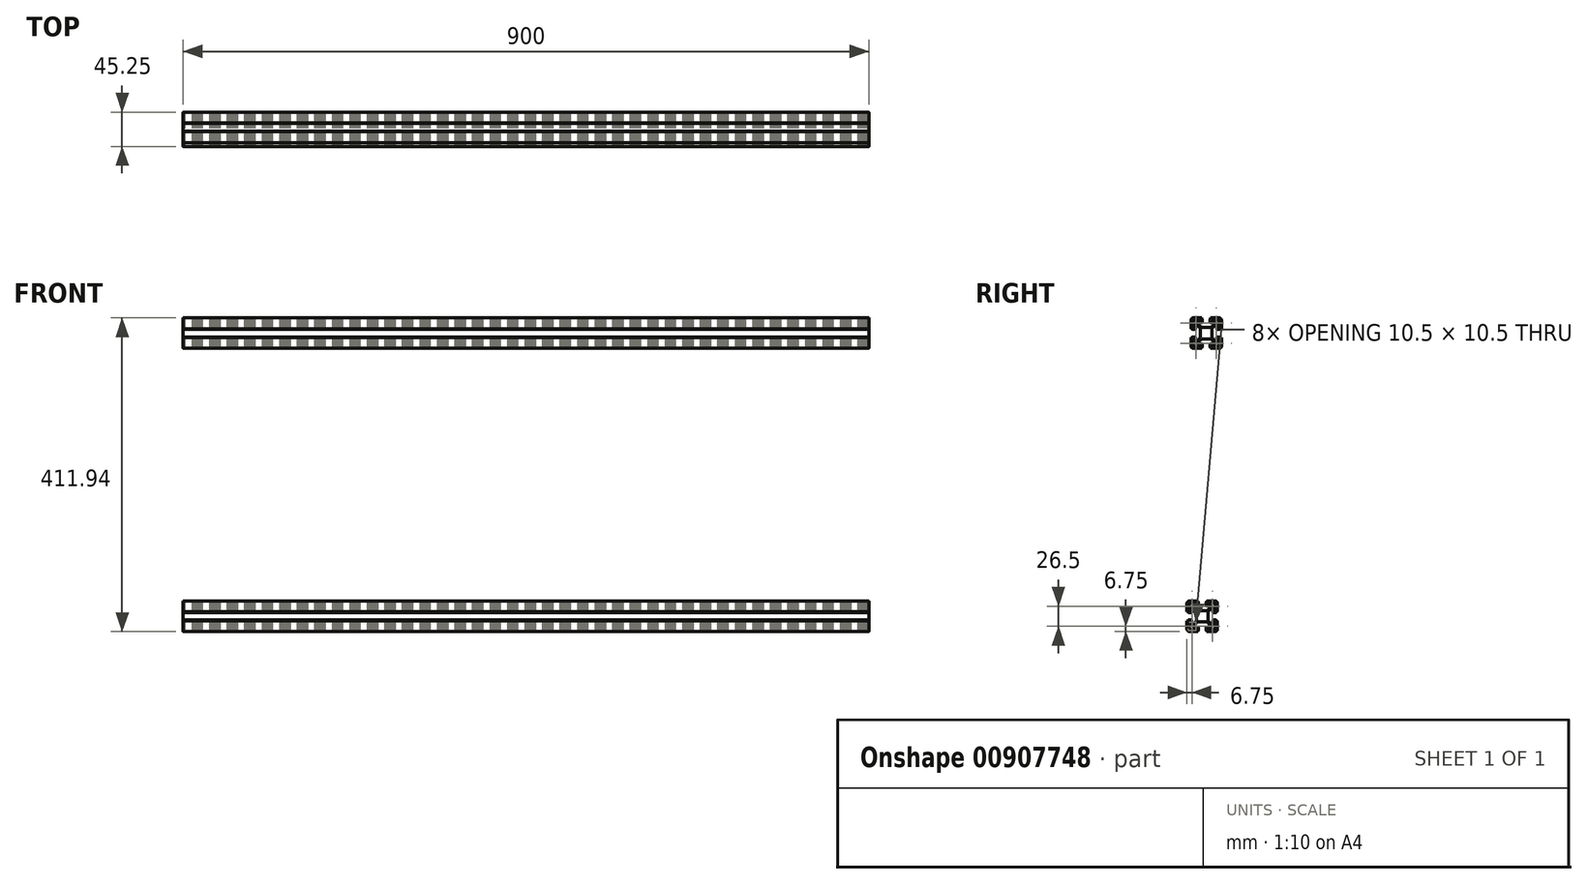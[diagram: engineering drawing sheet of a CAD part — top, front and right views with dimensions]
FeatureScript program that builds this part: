
annotation { "Feature Type Name" : "Feature", "Feature Type Description" : "" }
export const myFeature = defineFeature(function(context is Context, id is Id, definition is map)
    precondition{}
    {
        {
            var Q0;
            Q0=qCreatedBy(makeId("Right.planeOp"),FACE);
            var sketch = newSketch(context, id + "F0", { "sketchPlane" : qUnion([Q0])});
            skLineSegment(sketch, "E0", {"start": v(5.8, -18.5) * mm, "end": v(5.8, -20) * mm});
            skLineSegment(sketch, "E1", {"start": v(5.8, -20) * mm, "end": v(17, -20) * mm});
            skArc(sketch, "E2", {"start": v(17, -20) * mm, "mid": v(19.12, -19.12) * mm, "end": v(20, -17) * mm});
            skLineSegment(sketch, "E3", {"start": v(20, -17) * mm, "end": v(20, -5.8) * mm});
            skLineSegment(sketch, "E4", {"start": v(20, -5.8) * mm, "end": v(18.5, -5.8) * mm});
            skLineSegment(sketch, "E5", {"start": v(18.5, -5.8) * mm, "end": v(18.5, -5) * mm});
            skLineSegment(sketch, "E6", {"start": v(18.5, -5) * mm, "end": v(14, -5) * mm});
            skLineSegment(sketch, "E7", {"start": v(14, -5) * mm, "end": v(14, -10.05) * mm});
            skLineSegment(sketch, "E8", {"start": v(14, -10.05) * mm, "end": v(11.46, -10.05) * mm});
            skLineSegment(sketch, "E9", {"start": v(11.46, -10.05) * mm, "end": v(7.5, -6.09) * mm});
            skLineSegment(sketch, "E10", {"start": v(7.5, -6.09) * mm, "end": v(7.5, 6.09) * mm});
            skLineSegment(sketch, "E11", {"start": v(7.5, 6.09) * mm, "end": v(11.46, 10.05) * mm});
            skLineSegment(sketch, "E12", {"start": v(11.46, 10.05) * mm, "end": v(14, 10.05) * mm});
            skLineSegment(sketch, "E13", {"start": v(14, 10.05) * mm, "end": v(14, 5) * mm});
            skLineSegment(sketch, "E14", {"start": v(14, 5) * mm, "end": v(18.5, 5) * mm});
            skLineSegment(sketch, "E15", {"start": v(18.5, 5) * mm, "end": v(18.5, 5.8) * mm});
            skLineSegment(sketch, "E16", {"start": v(18.5, 5.8) * mm, "end": v(20, 5.8) * mm});
            skLineSegment(sketch, "E17", {"start": v(20, 5.8) * mm, "end": v(20, 17) * mm});
            skArc(sketch, "E18", {"start": v(20, 17) * mm, "mid": v(19.12, 19.12) * mm, "end": v(17, 20) * mm});
            skLineSegment(sketch, "E19", {"start": v(17, 20) * mm, "end": v(5.8, 20) * mm});
            skLineSegment(sketch, "E20", {"start": v(5.8, 20) * mm, "end": v(5.8, 18.5) * mm});
            skLineSegment(sketch, "E21", {"start": v(5.8, 18.5) * mm, "end": v(5, 18.5) * mm});
            skLineSegment(sketch, "E22", {"start": v(5, 18.5) * mm, "end": v(5, 14) * mm});
            skLineSegment(sketch, "E23", {"start": v(5, 14) * mm, "end": v(10.05, 14) * mm});
            skLineSegment(sketch, "E24", {"start": v(10.05, 14) * mm, "end": v(10.05, 11.46) * mm});
            skLineSegment(sketch, "E25", {"start": v(10.05, 11.46) * mm, "end": v(6.09, 7.5) * mm});
            skLineSegment(sketch, "E26", {"start": v(6.09, 7.5) * mm, "end": v(-6.09, 7.5) * mm});
            skLineSegment(sketch, "E27", {"start": v(-6.09, 7.5) * mm, "end": v(-10.05, 11.46) * mm});
            skLineSegment(sketch, "E28", {"start": v(-10.05, 11.46) * mm, "end": v(-10.05, 14) * mm});
            skLineSegment(sketch, "E29", {"start": v(-10.05, 14) * mm, "end": v(-5, 14) * mm});
            skLineSegment(sketch, "E30", {"start": v(-5, 14) * mm, "end": v(-5, 18.5) * mm});
            skLineSegment(sketch, "E31", {"start": v(-5, 18.5) * mm, "end": v(-5.8, 18.5) * mm});
            skLineSegment(sketch, "E32", {"start": v(-5.8, 18.5) * mm, "end": v(-5.8, 20) * mm});
            skLineSegment(sketch, "E33", {"start": v(-5.8, 20) * mm, "end": v(-17, 20) * mm});
            skArc(sketch, "E34", {"start": v(-17, 20) * mm, "mid": v(-19.12, 19.12) * mm, "end": v(-20, 17) * mm});
            skLineSegment(sketch, "E35", {"start": v(-20, 17) * mm, "end": v(-20, 5.8) * mm});
            skLineSegment(sketch, "E36", {"start": v(-20, 5.8) * mm, "end": v(-18.5, 5.8) * mm});
            skLineSegment(sketch, "E37", {"start": v(-18.5, 5.8) * mm, "end": v(-18.5, 5) * mm});
            skLineSegment(sketch, "E38", {"start": v(-18.5, 5) * mm, "end": v(-14, 5) * mm});
            skLineSegment(sketch, "E39", {"start": v(-14, 5) * mm, "end": v(-14, 10.05) * mm});
            skLineSegment(sketch, "E40", {"start": v(-14, 10.05) * mm, "end": v(-11.46, 10.05) * mm});
            skLineSegment(sketch, "E41", {"start": v(-11.46, 10.05) * mm, "end": v(-7.5, 6.09) * mm});
            skLineSegment(sketch, "E42", {"start": v(-7.5, 6.09) * mm, "end": v(-7.5, -6.09) * mm});
            skLineSegment(sketch, "E43", {"start": v(-7.5, -6.09) * mm, "end": v(-11.46, -10.05) * mm});
            skLineSegment(sketch, "E44", {"start": v(-11.46, -10.05) * mm, "end": v(-14, -10.05) * mm});
            skLineSegment(sketch, "E45", {"start": v(-14, -10.05) * mm, "end": v(-14, -5) * mm});
            skLineSegment(sketch, "E46", {"start": v(-14, -5) * mm, "end": v(-18.5, -5) * mm});
            skLineSegment(sketch, "E47", {"start": v(-18.5, -5) * mm, "end": v(-18.5, -5.8) * mm});
            skLineSegment(sketch, "E48", {"start": v(-18.5, -5.8) * mm, "end": v(-20, -5.8) * mm});
            skLineSegment(sketch, "E49", {"start": v(-20, -5.8) * mm, "end": v(-20, -17) * mm});
            skArc(sketch, "E50", {"start": v(-20, -17) * mm, "mid": v(-19.12, -19.12) * mm, "end": v(-17, -20) * mm});
            skLineSegment(sketch, "E51", {"start": v(-17, -20) * mm, "end": v(-5.8, -20) * mm});
            skLineSegment(sketch, "E52", {"start": v(-5.8, -20) * mm, "end": v(-5.8, -18.5) * mm});
            skLineSegment(sketch, "E53", {"start": v(-5.8, -18.5) * mm, "end": v(-5, -18.5) * mm});
            skLineSegment(sketch, "E54", {"start": v(-5, -18.5) * mm, "end": v(-5, -14) * mm});
            skLineSegment(sketch, "E55", {"start": v(-5, -14) * mm, "end": v(-10.05, -14) * mm});
            skLineSegment(sketch, "E56", {"start": v(-10.05, -14) * mm, "end": v(-10.05, -11.46) * mm});
            skLineSegment(sketch, "E57", {"start": v(-10.05, -11.46) * mm, "end": v(-6.09, -7.5) * mm});
            skLineSegment(sketch, "E58", {"start": v(-6.09, -7.5) * mm, "end": v(6.09, -7.5) * mm});
            skLineSegment(sketch, "E59", {"start": v(6.09, -7.5) * mm, "end": v(10.05, -11.46) * mm});
            skLineSegment(sketch, "E60", {"start": v(10.05, -11.46) * mm, "end": v(10.05, -14) * mm});
            skLineSegment(sketch, "E61", {"start": v(10.05, -14) * mm, "end": v(5, -14) * mm});
            skLineSegment(sketch, "E62", {"start": v(5, -14) * mm, "end": v(5, -18.5) * mm});
            skLineSegment(sketch, "E63", {"start": v(5, -18.5) * mm, "end": v(5.8, -18.5) * mm});
            skLineSegment(sketch, "E64", {"start": v(18.5, 9.5) * mm, "end": v(18.5, 14.5) * mm});
            skArc(sketch, "E65", {"start": v(15.5, 9.5) * mm, "mid": v(17, 8) * mm, "end": v(18.5, 9.5) * mm});
            skLineSegment(sketch, "E66", {"start": v(15.5, 11.75) * mm, "end": v(15.5, 9.5) * mm});
            skLineSegment(sketch, "E67", {"start": v(14.5, 11.75) * mm, "end": v(15.5, 11.75) * mm});
            skArc(sketch, "E68", {"start": v(11.75, 14.5) * mm, "mid": v(12.56, 12.56) * mm, "end": v(14.5, 11.75) * mm});
            skLineSegment(sketch, "E69", {"start": v(11.75, 15.5) * mm, "end": v(11.75, 14.5) * mm});
            skLineSegment(sketch, "E70", {"start": v(9.5, 15.5) * mm, "end": v(11.75, 15.5) * mm});
            skArc(sketch, "E71", {"start": v(9.5, 18.5) * mm, "mid": v(8, 17) * mm, "end": v(9.5, 15.5) * mm});
            skLineSegment(sketch, "E72", {"start": v(14.5, 18.5) * mm, "end": v(9.5, 18.5) * mm});
            skLineSegment(sketch, "E73", {"start": v(14.5, 17.25) * mm, "end": v(14.5, 18.5) * mm});
            skArc(sketch, "E74", {"start": v(17.25, 14.5) * mm, "mid": v(16.44, 16.44) * mm, "end": v(14.5, 17.25) * mm});
            skLineSegment(sketch, "E75", {"start": v(18.5, 14.5) * mm, "end": v(17.25, 14.5) * mm});
            skLineSegment(sketch, "E76", {"start": v(11.75, -14.5) * mm, "end": v(11.75, -15.5) * mm});
            skArc(sketch, "E77", {"start": v(14.5, -11.75) * mm, "mid": v(12.56, -12.56) * mm, "end": v(11.75, -14.5) * mm});
            skLineSegment(sketch, "E78", {"start": v(15.5, -11.75) * mm, "end": v(14.5, -11.75) * mm});
            skLineSegment(sketch, "E79", {"start": v(15.5, -9.5) * mm, "end": v(15.5, -11.75) * mm});
            skArc(sketch, "E80", {"start": v(18.5, -9.5) * mm, "mid": v(17, -8) * mm, "end": v(15.5, -9.5) * mm});
            skLineSegment(sketch, "E81", {"start": v(18.5, -14.5) * mm, "end": v(18.5, -9.5) * mm});
            skLineSegment(sketch, "E82", {"start": v(17.25, -14.5) * mm, "end": v(18.5, -14.5) * mm});
            skArc(sketch, "E83", {"start": v(14.5, -17.25) * mm, "mid": v(16.44, -16.44) * mm, "end": v(17.25, -14.5) * mm});
            skLineSegment(sketch, "E84", {"start": v(14.5, -18.5) * mm, "end": v(14.5, -17.25) * mm});
            skLineSegment(sketch, "E85", {"start": v(9.5, -18.5) * mm, "end": v(14.5, -18.5) * mm});
            skArc(sketch, "E86", {"start": v(9.5, -15.5) * mm, "mid": v(8, -17) * mm, "end": v(9.5, -18.5) * mm});
            skLineSegment(sketch, "E87", {"start": v(11.75, -15.5) * mm, "end": v(9.5, -15.5) * mm});
            skLineSegment(sketch, "E88", {"start": v(-2, 4.58) * mm, "end": v(-2.4, 5.5) * mm});
            skLineSegment(sketch, "E89", {"start": v(2.4, 5.5) * mm, "end": v(2, 4.58) * mm});
            skLineSegment(sketch, "E90", {"start": v(5.5, 5.5) * mm, "end": v(2.4, 5.5) * mm});
            skLineSegment(sketch, "E91", {"start": v(5.5, 2.4) * mm, "end": v(5.5, 5.5) * mm});
            skLineSegment(sketch, "E92", {"start": v(4.58, 2) * mm, "end": v(5.5, 2.4) * mm});
            skArc(sketch, "E93", {"start": v(4.58, -2) * mm, "mid": v(5, 0) * mm, "end": v(4.58, 2) * mm});
            skLineSegment(sketch, "E94", {"start": v(5.5, -2.4) * mm, "end": v(4.58, -2) * mm});
            skLineSegment(sketch, "E95", {"start": v(5.5, -5.5) * mm, "end": v(5.5, -2.4) * mm});
            skLineSegment(sketch, "E96", {"start": v(2.4, -5.5) * mm, "end": v(5.5, -5.5) * mm});
            skLineSegment(sketch, "E97", {"start": v(2, -4.58) * mm, "end": v(2.4, -5.5) * mm});
            skArc(sketch, "E98", {"start": v(-2, -4.58) * mm, "mid": v(0, -5) * mm, "end": v(2, -4.58) * mm});
            skLineSegment(sketch, "E99", {"start": v(-2.4, -5.5) * mm, "end": v(-2, -4.58) * mm});
            skLineSegment(sketch, "E100", {"start": v(-5.5, -5.5) * mm, "end": v(-2.4, -5.5) * mm});
            skLineSegment(sketch, "E101", {"start": v(-5.5, -2.4) * mm, "end": v(-5.5, -5.5) * mm});
            skLineSegment(sketch, "E102", {"start": v(-4.58, -2) * mm, "end": v(-5.5, -2.4) * mm});
            skArc(sketch, "E103", {"start": v(-4.58, 2) * mm, "mid": v(-5, 0) * mm, "end": v(-4.58, -2) * mm});
            skLineSegment(sketch, "E104", {"start": v(-5.5, 2.4) * mm, "end": v(-4.58, 2) * mm});
            skLineSegment(sketch, "E105", {"start": v(-5.5, 5.5) * mm, "end": v(-5.5, 2.4) * mm});
            skLineSegment(sketch, "E106", {"start": v(-2.4, 5.5) * mm, "end": v(-5.5, 5.5) * mm});
            skLineSegment(sketch, "E107", {"start": v(-18.5, -9.5) * mm, "end": v(-18.5, -14.5) * mm});
            skArc(sketch, "E108", {"start": v(-15.5, -9.5) * mm, "mid": v(-17, -8) * mm, "end": v(-18.5, -9.5) * mm});
            skLineSegment(sketch, "E109", {"start": v(-15.5, -11.75) * mm, "end": v(-15.5, -9.5) * mm});
            skLineSegment(sketch, "E110", {"start": v(-14.5, -11.75) * mm, "end": v(-15.5, -11.75) * mm});
            skArc(sketch, "E111", {"start": v(-11.75, -14.5) * mm, "mid": v(-12.56, -12.56) * mm, "end": v(-14.5, -11.75) * mm});
            skLineSegment(sketch, "E112", {"start": v(-11.75, -15.5) * mm, "end": v(-11.75, -14.5) * mm});
            skLineSegment(sketch, "E113", {"start": v(-9.5, -15.5) * mm, "end": v(-11.75, -15.5) * mm});
            skArc(sketch, "E114", {"start": v(-9.5, -18.5) * mm, "mid": v(-8, -17) * mm, "end": v(-9.5, -15.5) * mm});
            skLineSegment(sketch, "E115", {"start": v(-14.5, -18.5) * mm, "end": v(-9.5, -18.5) * mm});
            skLineSegment(sketch, "E116", {"start": v(-14.5, -17.25) * mm, "end": v(-14.5, -18.5) * mm});
            skArc(sketch, "E117", {"start": v(-17.25, -14.5) * mm, "mid": v(-16.44, -16.44) * mm, "end": v(-14.5, -17.25) * mm});
            skLineSegment(sketch, "E118", {"start": v(-18.5, -14.5) * mm, "end": v(-17.25, -14.5) * mm});
            skLineSegment(sketch, "E119", {"start": v(-11.75, 14.5) * mm, "end": v(-11.75, 15.5) * mm});
            skArc(sketch, "E120", {"start": v(-14.5, 11.75) * mm, "mid": v(-12.56, 12.56) * mm, "end": v(-11.75, 14.5) * mm});
            skLineSegment(sketch, "E121", {"start": v(-15.5, 11.75) * mm, "end": v(-14.5, 11.75) * mm});
            skLineSegment(sketch, "E122", {"start": v(-15.5, 9.5) * mm, "end": v(-15.5, 11.75) * mm});
            skArc(sketch, "E123", {"start": v(-18.5, 9.5) * mm, "mid": v(-17, 8) * mm, "end": v(-15.5, 9.5) * mm});
            skLineSegment(sketch, "E124", {"start": v(-18.5, 14.5) * mm, "end": v(-18.5, 9.5) * mm});
            skLineSegment(sketch, "E125", {"start": v(-17.25, 14.5) * mm, "end": v(-18.5, 14.5) * mm});
            skArc(sketch, "E126", {"start": v(-14.5, 17.25) * mm, "mid": v(-16.44, 16.44) * mm, "end": v(-17.25, 14.5) * mm});
            skLineSegment(sketch, "E127", {"start": v(-14.5, 18.5) * mm, "end": v(-14.5, 17.25) * mm});
            skLineSegment(sketch, "E128", {"start": v(-9.5, 18.5) * mm, "end": v(-14.5, 18.5) * mm});
            skArc(sketch, "E129", {"start": v(-9.5, 15.5) * mm, "mid": v(-8, 17) * mm, "end": v(-9.5, 18.5) * mm});
            skLineSegment(sketch, "E130", {"start": v(-11.75, 15.5) * mm, "end": v(-9.5, 15.5) * mm});
            skLineSegment(sketch, "E131", {"start": v(11.05, 353.44) * mm, "end": v(11.05, 351.94) * mm});
            skLineSegment(sketch, "E132", {"start": v(11.05, 351.94) * mm, "end": v(22.25, 351.94) * mm});
            skArc(sketch, "E133", {"start": v(22.25, 351.94) * mm, "mid": v(24.37, 352.82) * mm, "end": v(25.25, 354.94) * mm});
            skLineSegment(sketch, "E134", {"start": v(25.25, 354.94) * mm, "end": v(25.25, 366.14) * mm});
            skLineSegment(sketch, "E135", {"start": v(25.25, 366.14) * mm, "end": v(23.75, 366.14) * mm});
            skLineSegment(sketch, "E136", {"start": v(23.75, 366.14) * mm, "end": v(23.75, 366.94) * mm});
            skLineSegment(sketch, "E137", {"start": v(23.75, 366.94) * mm, "end": v(19.25, 366.94) * mm});
            skLineSegment(sketch, "E138", {"start": v(19.25, 366.94) * mm, "end": v(19.25, 361.89) * mm});
            skLineSegment(sketch, "E139", {"start": v(19.25, 361.89) * mm, "end": v(16.71, 361.89) * mm});
            skLineSegment(sketch, "E140", {"start": v(16.71, 361.89) * mm, "end": v(12.75, 365.85) * mm});
            skLineSegment(sketch, "E141", {"start": v(12.75, 365.85) * mm, "end": v(12.75, 378.02) * mm});
            skLineSegment(sketch, "E142", {"start": v(12.75, 378.02) * mm, "end": v(16.71, 381.99) * mm});
            skLineSegment(sketch, "E143", {"start": v(16.71, 381.99) * mm, "end": v(19.25, 381.99) * mm});
            skLineSegment(sketch, "E144", {"start": v(19.25, 381.99) * mm, "end": v(19.25, 376.94) * mm});
            skLineSegment(sketch, "E145", {"start": v(19.25, 376.94) * mm, "end": v(23.75, 376.94) * mm});
            skLineSegment(sketch, "E146", {"start": v(23.75, 376.94) * mm, "end": v(23.75, 377.74) * mm});
            skLineSegment(sketch, "E147", {"start": v(23.75, 377.74) * mm, "end": v(25.25, 377.74) * mm});
            skLineSegment(sketch, "E148", {"start": v(25.25, 377.74) * mm, "end": v(25.25, 388.94) * mm});
            skArc(sketch, "E149", {"start": v(25.25, 388.94) * mm, "mid": v(24.37, 391.06) * mm, "end": v(22.25, 391.94) * mm});
            skLineSegment(sketch, "E150", {"start": v(22.25, 391.94) * mm, "end": v(11.05, 391.94) * mm});
            skLineSegment(sketch, "E151", {"start": v(11.05, 391.94) * mm, "end": v(11.05, 390.44) * mm});
            skLineSegment(sketch, "E152", {"start": v(11.05, 390.44) * mm, "end": v(10.25, 390.44) * mm});
            skLineSegment(sketch, "E153", {"start": v(10.25, 390.44) * mm, "end": v(10.25, 385.94) * mm});
            skLineSegment(sketch, "E154", {"start": v(10.25, 385.94) * mm, "end": v(15.3, 385.94) * mm});
            skLineSegment(sketch, "E155", {"start": v(15.3, 385.94) * mm, "end": v(15.3, 383.4) * mm});
            skLineSegment(sketch, "E156", {"start": v(15.3, 383.4) * mm, "end": v(11.34, 379.44) * mm});
            skLineSegment(sketch, "E157", {"start": v(11.34, 379.44) * mm, "end": v(-0.84, 379.44) * mm});
            skLineSegment(sketch, "E158", {"start": v(-0.84, 379.44) * mm, "end": v(-4.8, 383.4) * mm});
            skLineSegment(sketch, "E159", {"start": v(-4.8, 383.4) * mm, "end": v(-4.8, 385.94) * mm});
            skLineSegment(sketch, "E160", {"start": v(-4.8, 385.94) * mm, "end": v(0.25, 385.94) * mm});
            skLineSegment(sketch, "E161", {"start": v(0.25, 385.94) * mm, "end": v(0.25, 390.44) * mm});
            skLineSegment(sketch, "E162", {"start": v(0.25, 390.44) * mm, "end": v(-0.55, 390.44) * mm});
            skLineSegment(sketch, "E163", {"start": v(-0.55, 390.44) * mm, "end": v(-0.55, 391.94) * mm});
            skLineSegment(sketch, "E164", {"start": v(-0.55, 391.94) * mm, "end": v(-11.75, 391.94) * mm});
            skArc(sketch, "E165", {"start": v(-11.75, 391.94) * mm, "mid": v(-13.87, 391.06) * mm, "end": v(-14.75, 388.94) * mm});
            skLineSegment(sketch, "E166", {"start": v(-14.75, 388.94) * mm, "end": v(-14.75, 377.74) * mm});
            skLineSegment(sketch, "E167", {"start": v(-14.75, 377.74) * mm, "end": v(-13.25, 377.74) * mm});
            skLineSegment(sketch, "E168", {"start": v(-13.25, 377.74) * mm, "end": v(-13.25, 376.94) * mm});
            skLineSegment(sketch, "E169", {"start": v(-13.25, 376.94) * mm, "end": v(-8.75, 376.94) * mm});
            skLineSegment(sketch, "E170", {"start": v(-8.75, 376.94) * mm, "end": v(-8.75, 381.99) * mm});
            skLineSegment(sketch, "E171", {"start": v(-8.75, 381.99) * mm, "end": v(-6.21, 381.99) * mm});
            skLineSegment(sketch, "E172", {"start": v(-6.21, 381.99) * mm, "end": v(-2.25, 378.02) * mm});
            skLineSegment(sketch, "E173", {"start": v(-2.25, 378.02) * mm, "end": v(-2.25, 365.85) * mm});
            skLineSegment(sketch, "E174", {"start": v(-2.25, 365.85) * mm, "end": v(-6.21, 361.89) * mm});
            skLineSegment(sketch, "E175", {"start": v(-6.21, 361.89) * mm, "end": v(-8.75, 361.89) * mm});
            skLineSegment(sketch, "E176", {"start": v(-8.75, 361.89) * mm, "end": v(-8.75, 366.94) * mm});
            skLineSegment(sketch, "E177", {"start": v(-8.75, 366.94) * mm, "end": v(-13.25, 366.94) * mm});
            skLineSegment(sketch, "E178", {"start": v(-13.25, 366.94) * mm, "end": v(-13.25, 366.14) * mm});
            skLineSegment(sketch, "E179", {"start": v(-13.25, 366.14) * mm, "end": v(-14.75, 366.14) * mm});
            skLineSegment(sketch, "E180", {"start": v(-14.75, 366.14) * mm, "end": v(-14.75, 354.94) * mm});
            skArc(sketch, "E181", {"start": v(-14.75, 354.94) * mm, "mid": v(-13.87, 352.82) * mm, "end": v(-11.75, 351.94) * mm});
            skLineSegment(sketch, "E182", {"start": v(-11.75, 351.94) * mm, "end": v(-0.55, 351.94) * mm});
            skLineSegment(sketch, "E183", {"start": v(-0.55, 351.94) * mm, "end": v(-0.55, 353.44) * mm});
            skLineSegment(sketch, "E184", {"start": v(-0.55, 353.44) * mm, "end": v(0.25, 353.44) * mm});
            skLineSegment(sketch, "E185", {"start": v(0.25, 353.44) * mm, "end": v(0.25, 357.94) * mm});
            skLineSegment(sketch, "E186", {"start": v(0.25, 357.94) * mm, "end": v(-4.8, 357.94) * mm});
            skLineSegment(sketch, "E187", {"start": v(-4.8, 357.94) * mm, "end": v(-4.8, 360.47) * mm});
            skLineSegment(sketch, "E188", {"start": v(-4.8, 360.47) * mm, "end": v(-0.84, 364.44) * mm});
            skLineSegment(sketch, "E189", {"start": v(-0.84, 364.44) * mm, "end": v(11.34, 364.44) * mm});
            skLineSegment(sketch, "E190", {"start": v(11.34, 364.44) * mm, "end": v(15.3, 360.47) * mm});
            skLineSegment(sketch, "E191", {"start": v(15.3, 360.47) * mm, "end": v(15.3, 357.94) * mm});
            skLineSegment(sketch, "E192", {"start": v(15.3, 357.94) * mm, "end": v(10.25, 357.94) * mm});
            skLineSegment(sketch, "E193", {"start": v(10.25, 357.94) * mm, "end": v(10.25, 353.44) * mm});
            skLineSegment(sketch, "E194", {"start": v(10.25, 353.44) * mm, "end": v(11.05, 353.44) * mm});
            skLineSegment(sketch, "E195", {"start": v(23.75, 381.44) * mm, "end": v(23.75, 386.44) * mm});
            skArc(sketch, "E196", {"start": v(20.75, 381.44) * mm, "mid": v(22.25, 379.94) * mm, "end": v(23.75, 381.44) * mm});
            skLineSegment(sketch, "E197", {"start": v(20.75, 383.69) * mm, "end": v(20.75, 381.44) * mm});
            skLineSegment(sketch, "E198", {"start": v(19.75, 383.69) * mm, "end": v(20.75, 383.69) * mm});
            skArc(sketch, "E199", {"start": v(17, 386.44) * mm, "mid": v(17.8, 384.5) * mm, "end": v(19.75, 383.69) * mm});
            skLineSegment(sketch, "E200", {"start": v(17, 387.44) * mm, "end": v(17, 386.44) * mm});
            skLineSegment(sketch, "E201", {"start": v(14.75, 387.44) * mm, "end": v(17, 387.44) * mm});
            skArc(sketch, "E202", {"start": v(14.75, 390.44) * mm, "mid": v(13.25, 388.94) * mm, "end": v(14.75, 387.44) * mm});
            skLineSegment(sketch, "E203", {"start": v(19.75, 390.44) * mm, "end": v(14.75, 390.44) * mm});
            skLineSegment(sketch, "E204", {"start": v(19.75, 389.19) * mm, "end": v(19.75, 390.44) * mm});
            skArc(sketch, "E205", {"start": v(22.5, 386.44) * mm, "mid": v(21.7, 388.38) * mm, "end": v(19.75, 389.19) * mm});
            skLineSegment(sketch, "E206", {"start": v(23.75, 386.44) * mm, "end": v(22.5, 386.44) * mm});
            skLineSegment(sketch, "E207", {"start": v(17, 357.44) * mm, "end": v(17, 356.44) * mm});
            skArc(sketch, "E208", {"start": v(19.75, 360.19) * mm, "mid": v(17.8, 359.38) * mm, "end": v(17, 357.44) * mm});
            skLineSegment(sketch, "E209", {"start": v(20.75, 360.19) * mm, "end": v(19.75, 360.19) * mm});
            skLineSegment(sketch, "E210", {"start": v(20.75, 362.44) * mm, "end": v(20.75, 360.19) * mm});
            skArc(sketch, "E211", {"start": v(23.75, 362.44) * mm, "mid": v(22.25, 363.94) * mm, "end": v(20.75, 362.44) * mm});
            skLineSegment(sketch, "E212", {"start": v(23.75, 357.44) * mm, "end": v(23.75, 362.44) * mm});
            skLineSegment(sketch, "E213", {"start": v(22.5, 357.44) * mm, "end": v(23.75, 357.44) * mm});
            skArc(sketch, "E214", {"start": v(19.75, 354.69) * mm, "mid": v(21.7, 355.5) * mm, "end": v(22.5, 357.44) * mm});
            skLineSegment(sketch, "E215", {"start": v(19.75, 353.44) * mm, "end": v(19.75, 354.69) * mm});
            skLineSegment(sketch, "E216", {"start": v(14.75, 353.44) * mm, "end": v(19.75, 353.44) * mm});
            skArc(sketch, "E217", {"start": v(14.75, 356.44) * mm, "mid": v(13.25, 354.94) * mm, "end": v(14.75, 353.44) * mm});
            skLineSegment(sketch, "E218", {"start": v(17, 356.44) * mm, "end": v(14.75, 356.44) * mm});
            skLineSegment(sketch, "E219", {"start": v(3.25, 376.52) * mm, "end": v(2.85, 377.44) * mm});
            skLineSegment(sketch, "E220", {"start": v(7.65, 377.44) * mm, "end": v(7.25, 376.52) * mm});
            skLineSegment(sketch, "E221", {"start": v(10.75, 377.44) * mm, "end": v(7.65, 377.44) * mm});
            skLineSegment(sketch, "E222", {"start": v(10.75, 374.34) * mm, "end": v(10.75, 377.44) * mm});
            skLineSegment(sketch, "E223", {"start": v(9.83, 373.94) * mm, "end": v(10.75, 374.34) * mm});
            skArc(sketch, "E224", {"start": v(9.83, 369.94) * mm, "mid": v(10.25, 371.94) * mm, "end": v(9.83, 373.94) * mm});
            skLineSegment(sketch, "E225", {"start": v(10.75, 369.54) * mm, "end": v(9.83, 369.94) * mm});
            skLineSegment(sketch, "E226", {"start": v(10.75, 366.44) * mm, "end": v(10.75, 369.54) * mm});
            skLineSegment(sketch, "E227", {"start": v(7.65, 366.44) * mm, "end": v(10.75, 366.44) * mm});
            skLineSegment(sketch, "E228", {"start": v(7.25, 367.36) * mm, "end": v(7.65, 366.44) * mm});
            skArc(sketch, "E229", {"start": v(3.25, 367.36) * mm, "mid": v(5.25, 366.94) * mm, "end": v(7.25, 367.36) * mm});
            skLineSegment(sketch, "E230", {"start": v(2.85, 366.44) * mm, "end": v(3.25, 367.36) * mm});
            skLineSegment(sketch, "E231", {"start": v(-0.25, 366.44) * mm, "end": v(2.85, 366.44) * mm});
            skLineSegment(sketch, "E232", {"start": v(-0.25, 369.54) * mm, "end": v(-0.25, 366.44) * mm});
            skLineSegment(sketch, "E233", {"start": v(0.67, 369.94) * mm, "end": v(-0.25, 369.54) * mm});
            skArc(sketch, "E234", {"start": v(0.67, 373.94) * mm, "mid": v(0.25, 371.94) * mm, "end": v(0.67, 369.94) * mm});
            skLineSegment(sketch, "E235", {"start": v(-0.25, 374.34) * mm, "end": v(0.67, 373.94) * mm});
            skLineSegment(sketch, "E236", {"start": v(-0.25, 377.44) * mm, "end": v(-0.25, 374.34) * mm});
            skLineSegment(sketch, "E237", {"start": v(2.85, 377.44) * mm, "end": v(-0.25, 377.44) * mm});
            skLineSegment(sketch, "E238", {"start": v(-13.25, 362.44) * mm, "end": v(-13.25, 357.44) * mm});
            skArc(sketch, "E239", {"start": v(-10.25, 362.44) * mm, "mid": v(-11.75, 363.94) * mm, "end": v(-13.25, 362.44) * mm});
            skLineSegment(sketch, "E240", {"start": v(-10.25, 360.19) * mm, "end": v(-10.25, 362.44) * mm});
            skLineSegment(sketch, "E241", {"start": v(-9.25, 360.19) * mm, "end": v(-10.25, 360.19) * mm});
            skArc(sketch, "E242", {"start": v(-6.5, 357.44) * mm, "mid": v(-7.3, 359.38) * mm, "end": v(-9.25, 360.19) * mm});
            skLineSegment(sketch, "E243", {"start": v(-6.5, 356.44) * mm, "end": v(-6.5, 357.44) * mm});
            skLineSegment(sketch, "E244", {"start": v(-4.25, 356.44) * mm, "end": v(-6.5, 356.44) * mm});
            skArc(sketch, "E245", {"start": v(-4.25, 353.44) * mm, "mid": v(-2.75, 354.94) * mm, "end": v(-4.25, 356.44) * mm});
            skLineSegment(sketch, "E246", {"start": v(-9.25, 353.44) * mm, "end": v(-4.25, 353.44) * mm});
            skLineSegment(sketch, "E247", {"start": v(-9.25, 354.69) * mm, "end": v(-9.25, 353.44) * mm});
            skArc(sketch, "E248", {"start": v(-12, 357.44) * mm, "mid": v(-11.2, 355.5) * mm, "end": v(-9.25, 354.69) * mm});
            skLineSegment(sketch, "E249", {"start": v(-13.25, 357.44) * mm, "end": v(-12, 357.44) * mm});
            skLineSegment(sketch, "E250", {"start": v(-6.5, 386.44) * mm, "end": v(-6.5, 387.44) * mm});
            skArc(sketch, "E251", {"start": v(-9.25, 383.69) * mm, "mid": v(-7.3, 384.5) * mm, "end": v(-6.5, 386.44) * mm});
            skLineSegment(sketch, "E252", {"start": v(-10.25, 383.69) * mm, "end": v(-9.25, 383.69) * mm});
            skLineSegment(sketch, "E253", {"start": v(-10.25, 381.44) * mm, "end": v(-10.25, 383.69) * mm});
            skArc(sketch, "E254", {"start": v(-13.25, 381.44) * mm, "mid": v(-11.75, 379.94) * mm, "end": v(-10.25, 381.44) * mm});
            skLineSegment(sketch, "E255", {"start": v(-13.25, 386.44) * mm, "end": v(-13.25, 381.44) * mm});
            skLineSegment(sketch, "E256", {"start": v(-12, 386.44) * mm, "end": v(-13.25, 386.44) * mm});
            skArc(sketch, "E257", {"start": v(-9.25, 389.19) * mm, "mid": v(-11.2, 388.38) * mm, "end": v(-12, 386.44) * mm});
            skLineSegment(sketch, "E258", {"start": v(-9.25, 390.44) * mm, "end": v(-9.25, 389.19) * mm});
            skLineSegment(sketch, "E259", {"start": v(-4.25, 390.44) * mm, "end": v(-9.25, 390.44) * mm});
            skArc(sketch, "E260", {"start": v(-4.25, 387.44) * mm, "mid": v(-2.75, 388.94) * mm, "end": v(-4.25, 390.44) * mm});
            skLineSegment(sketch, "E261", {"start": v(-6.5, 387.44) * mm, "end": v(-4.25, 387.44) * mm});
            skSolve(sketch);
        }
        {
            var Q0;
            Q0 = qSketchRegion(id + "F0", true);
            extrude(context, id + "F1", {"entities" : qUnion([Q0]), "depth" : 900 * mm, "offsetDistance" : 25 * mm});
        }
    });
